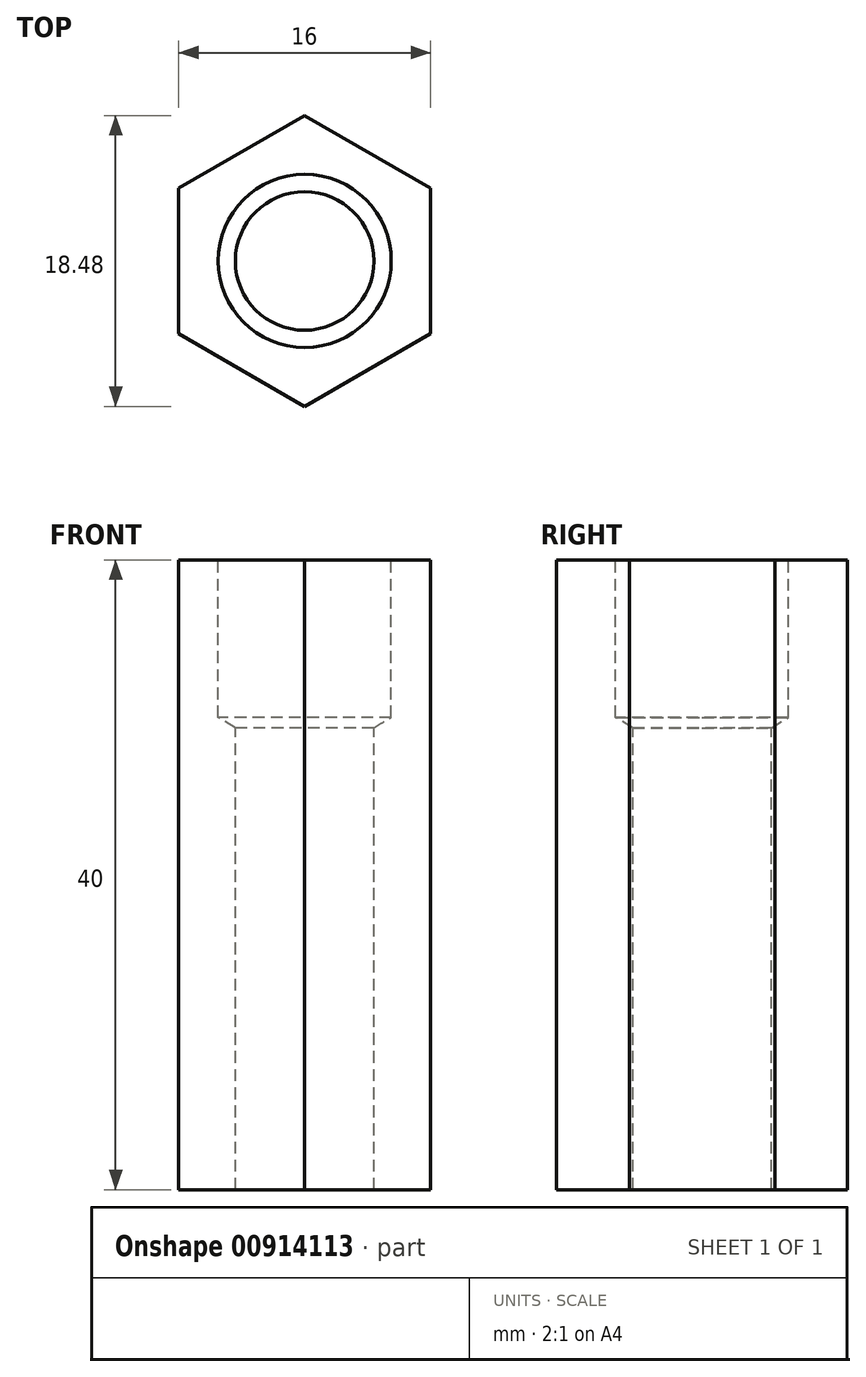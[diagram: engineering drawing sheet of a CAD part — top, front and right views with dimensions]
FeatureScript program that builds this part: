
annotation { "Feature Type Name" : "Feature", "Feature Type Description" : "" }
export const myFeature = defineFeature(function(context is Context, id is Id, definition is map)
    precondition{}
    {
        {
            var Q0;
            Q0=qCreatedBy(makeId("Top.planeOp"),FACE);
            var sketch = newSketch(context, id + "F0", { "sketchPlane" : qUnion([Q0])});
            skCircle(sketch, "E0.cCircle", {"center": v(0, 0) * mm, "radius": 8 * mm, "construction": true});
            skLineSegment(sketch, "E0.0", {"start": v(8, 4.62) * mm, "end": v(8, -4.62) * mm});
            skLineSegment(sketch, "E0.1", {"start": v(8, -4.62) * mm, "end": v(0, -9.24) * mm});
            skLineSegment(sketch, "E0.2", {"start": v(0, -9.24) * mm, "end": v(-8, -4.62) * mm});
            skLineSegment(sketch, "E0.3", {"start": v(-8, -4.62) * mm, "end": v(-8, 4.62) * mm});
            skLineSegment(sketch, "E0.4", {"start": v(-8, 4.62) * mm, "end": v(0, 9.24) * mm});
            skLineSegment(sketch, "E0.5", {"start": v(0, 9.24) * mm, "end": v(8, 4.62) * mm});
            skPoint(sketch, "E0.0.midPoint", {"position": v(8, 0) * mm});
            skSolve(sketch);
        }
        {
            var Q0;
            Q0 = qSketchRegion(id + "F0", true);
            extrude(context, id + "F1", {"entities" : qUnion([Q0]), "depth" : 40 * mm, "offsetDistance" : 25 * mm});
        }
        {
            var Q0;
            Q0=makeQuery(id+"F1.opExtrude","CAP_FACE",FACE,{"disambiguationData":[OSD([sQuery(id+"F0.wireOp",EDGE,"E0.0"),sQuery(id+"F0.wireOp",EDGE,"E0.1"),sQuery(id+"F0.wireOp",EDGE,"E0.2"),sQuery(id+"F0.wireOp",EDGE,"E0.3"),sQuery(id+"F0.wireOp",EDGE,"E0.4"),sQuery(id+"F0.wireOp",EDGE,"E0.5")])],"isStart":false});
            var sketch = newSketch(context, id + "F2", { "sketchPlane" : qUnion([Q0])});
            skPoint(sketch, "E1", {"position": v(0, 0) * mm});
            skSolve(sketch);
        }
        {
            var Q0;
            Q0=sQuery(id+"F2.wireOp",VERTEX,"E1");
            var Q1;
            Q1=makeQuery(id+"F1.opExtrude","SWEPT_BODY",BODY,{"disambiguationData":[OSD([sQuery(id+"F0.wireOp",EDGE,"E0.0"),sQuery(id+"F0.wireOp",EDGE,"E0.1"),sQuery(id+"F0.wireOp",EDGE,"E0.2"),sQuery(id+"F0.wireOp",EDGE,"E0.3"),sQuery(id+"F0.wireOp",EDGE,"E0.4"),sQuery(id+"F0.wireOp",EDGE,"E0.5")])]});
            hole(context, id + "F3", {"style" : HoleStyle.SIMPLE, "endStyle" : HoleEndStyle.BLIND, "standardTappedOrClearance" : lookupTablePath({ "fit" : "Normal", "standard" : "ISO", "size" : "M10", "type" : "Clearance" }), "standardBlindInLast" : lookupTablePath({ "fit" : "Normal", "standard" : "ISO", "engagement" : "75%", "pitch" : "1.5 mm", "size" : "M10", "type" : "Clearance & tapped" }), "holeDiameter" : 11 * mm, "majorDiameter" : 8 * mm, "holeDepth" : 10 * mm, "isTappedThrough" : true, "tappedDepth" : 14 * mm, "tapClearance" : 3, "locations" : qUnion([Q0]), "scope" : qUnion([Q1])});
        }
        {
            var Q0;
            Q0=sQuery(id+"F2.wireOp",VERTEX,"E1");
            var Q1;
            Q1=makeQuery(id+"F1.opExtrude","SWEPT_BODY",BODY,{"disambiguationData":[OSD([sQuery(id+"F0.wireOp",EDGE,"E0.0"),sQuery(id+"F0.wireOp",EDGE,"E0.1"),sQuery(id+"F0.wireOp",EDGE,"E0.2"),sQuery(id+"F0.wireOp",EDGE,"E0.3"),sQuery(id+"F0.wireOp",EDGE,"E0.4"),sQuery(id+"F0.wireOp",EDGE,"E0.5")])]});
            hole(context, id + "F4", {"style" : HoleStyle.SIMPLE, "endStyle" : HoleEndStyle.THROUGH, "standardTappedOrClearance" : lookupTablePath({ "standard" : "ISO", "engagement" : "75%", "pitch" : "1.25 mm", "size" : "M10", "type" : "Tapped" }), "standardBlindInLast" : lookupTablePath({ "standard" : "ISO", "fit" : "Normal", "engagement" : "75%", "pitch" : "1.25 mm", "size" : "M10", "type" : "Clearance & tapped" }), "holeDiameter" : 8.8 * mm, "majorDiameter" : 10 * mm, "showTappedDepth" : true, "isTappedThrough" : true, "tappedDepth" : 14 * mm, "tapClearance" : 3, "locations" : qUnion([Q0]), "scope" : qUnion([Q1])});
        }
    });
